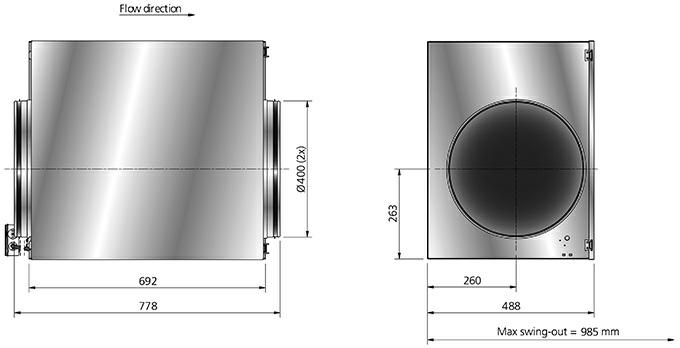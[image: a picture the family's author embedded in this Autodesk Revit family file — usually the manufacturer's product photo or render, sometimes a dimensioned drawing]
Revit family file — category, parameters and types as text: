
# Revit family: IRE 630 C3 ErP AC_
name_source: partatom
category: Mechanical Equipment
revit_build: Autodesk Revit MEP 2014 (Build: 20130308_1515(x64)
units: mm (PartAtom-declared; Revit-internal decimal feet)

## types (1)
- IRE 630 C3 ErP AC
    Capacitor = - μF
    Current = 5 A
    Depth = 955 mm  [stored 3.1332 ft]
    Description = Insulated duct fans with circular connections
    Diameter = 630 mm  [stored 2.06693 ft]
    Frequency = 50 Hz
    Height = 703 mm  [stored 2.30643 ft]
    Main Material = Steel, Galvanized
    Max. temperature of transported air = 75 °C
    Max. temperature of transported air when speed controlled = 60 °C
    Phase = 3
    Power = 2540 W
    Sound pressure level at 3 m = 45 dB(A)
    Speed = 890 rpm
    Voltage = 400 V
    Voltage range = 380-415 V
    Weight = 104.00 kg
    Width = 1067 mm  [stored 3.50066 ft]
    Wiring diagram = Y 4040004 / Δ 4040003

note: [stored X ft] marks values corroborated as IEEE doubles in the binary element streams (Revit-internal decimal feet)

## geometry (parser evidence)
native form markers: Sweep x5
no freeform markers — native parametric forms only
